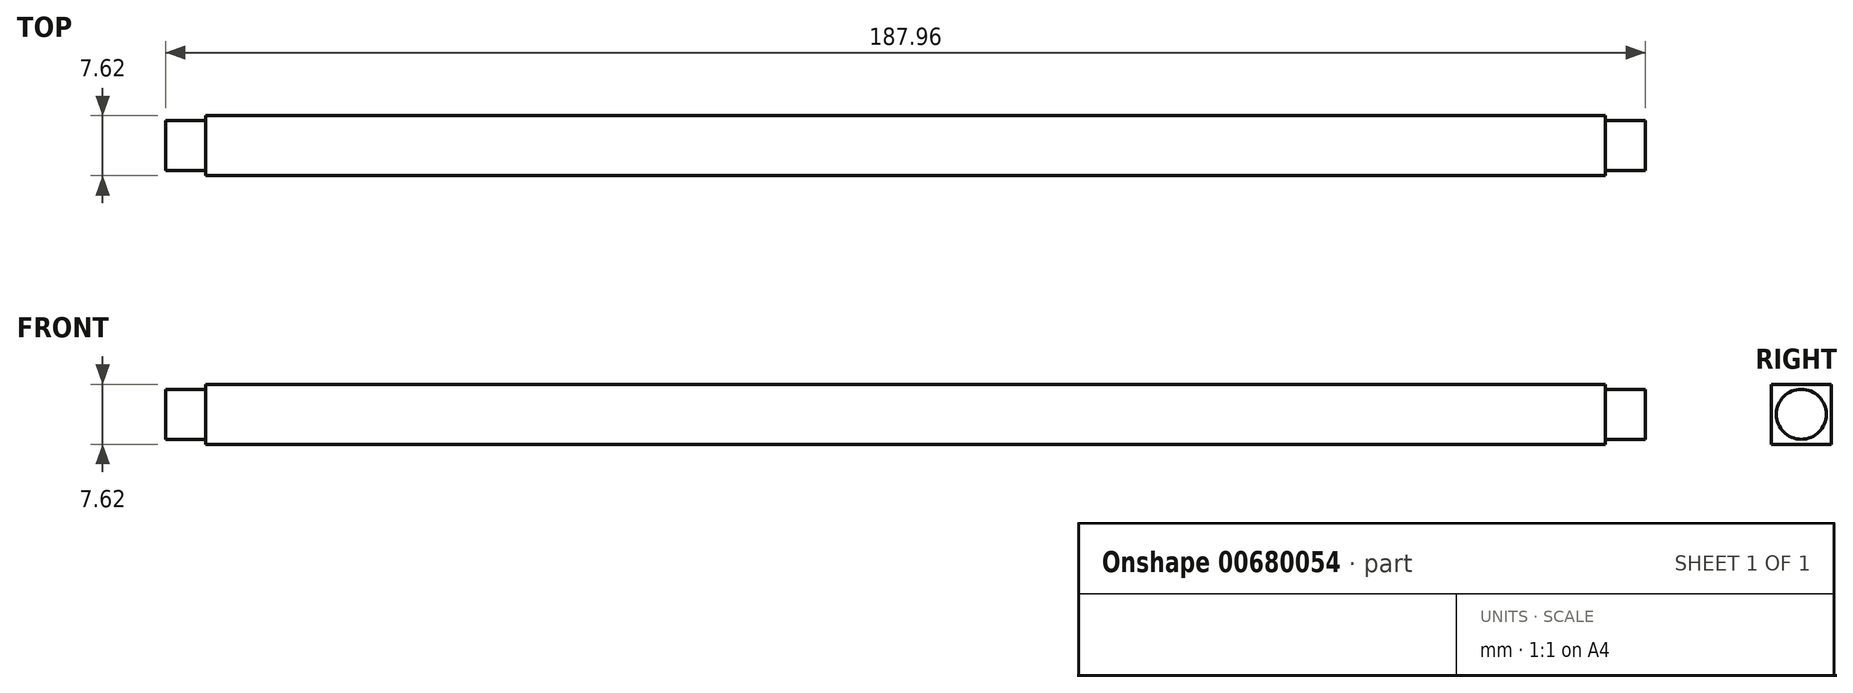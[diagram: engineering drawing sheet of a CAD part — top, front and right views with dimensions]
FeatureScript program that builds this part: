
annotation { "Feature Type Name" : "Feature", "Feature Type Description" : "" }
export const myFeature = defineFeature(function(context is Context, id is Id, definition is map)
    precondition{}
    {
        {
            var Q0;
            Q0=qCreatedBy(makeId("Top.planeOp"),FACE);
            var sketch = newSketch(context, id + "F0", { "sketchPlane" : qUnion([Q0])});
            skLineSegment(sketch, "E0.bottom", {"start": v(88.9, -3.8) * mm, "end": v(-88.9, -3.81) * mm});
            skLineSegment(sketch, "E0.top", {"start": v(88.9, 3.81) * mm, "end": v(-88.9, 3.8) * mm});
            skLineSegment(sketch, "E0.left", {"start": v(88.9, -3.8) * mm, "end": v(88.9, 3.81) * mm});
            skLineSegment(sketch, "E0.right", {"start": v(-88.9, -3.81) * mm, "end": v(-88.9, 3.8) * mm});
            skPoint(sketch, "E0.middle", {"position": v(0, 0) * mm});
            skSolve(sketch);
        }
        {
            var Q0;
            Q0 = qSketchRegion(id + "F0", true);
            extrude(context, id + "F1", {"entities" : qUnion([Q0]), "depth" : 7.62 * mm, "offsetDistance" : 25.4 * mm});
        }
        {
            var Q0;
            Q0=makeQuery(id+"F1.opExtrude","SWEPT_FACE",FACE,{"disambiguationData":[OSD([sQuery(id+"F0.wireOp",EDGE,"E0.left")])]});
            var sketch = newSketch(context, id + "F2", { "sketchPlane" : qUnion([Q0])});
            skCircle(sketch, "E1", {"center": v(0, 3.81) * mm, "radius": 3.18 * mm});
            skSolve(sketch);
        }
        {
            var Q0;
            Q0 = qSketchRegion(id + "F2", true);
            extrude(context, id + "F3", {"entities" : qUnion([Q0]), "operationType" : NewBodyOperationType.ADD, "depth" : 5.08 * mm, "offsetDistance" : 25.4 * mm});
        }
        {
            var Q0;
            Q0=makeQuery(id+"F1.opExtrude","SWEPT_FACE",FACE,{"disambiguationData":[OSD([sQuery(id+"F0.wireOp",EDGE,"E0.right")])]});
            var sketch = newSketch(context, id + "F4", { "sketchPlane" : qUnion([Q0])});
            skCircle(sketch, "E2", {"center": v(0, 3.81) * mm, "radius": 3.18 * mm});
            skSolve(sketch);
        }
        {
            var Q0;
            Q0 = qSketchRegion(id + "F4", true);
            extrude(context, id + "F5", {"entities" : qUnion([Q0]), "operationType" : NewBodyOperationType.ADD, "depth" : 5.08 * mm, "offsetDistance" : 25.4 * mm});
        }
    });
